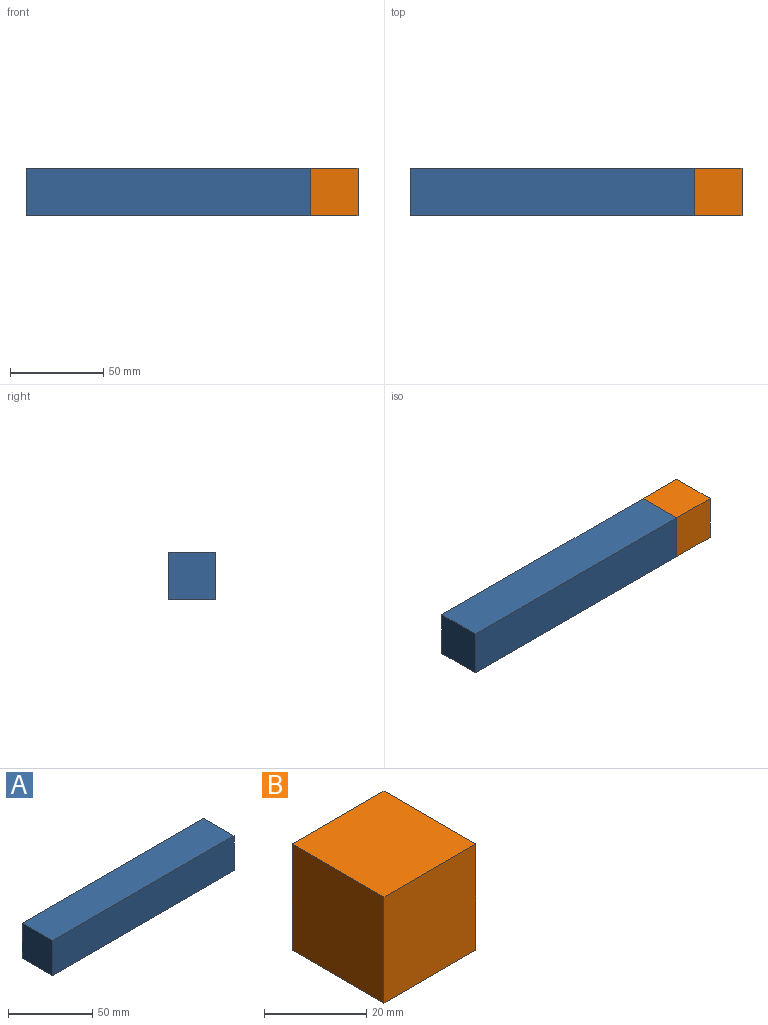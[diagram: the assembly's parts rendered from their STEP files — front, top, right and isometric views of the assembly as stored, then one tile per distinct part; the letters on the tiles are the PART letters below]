
ASSEMBLY  parts=2 mates=1
PART A: 6 faces, bbox 152.4x25.4x25.4 mm
  f0: plane 152.4x25.4mm, normal (0,0,1), area 3871mm2, adj f1,f3,f4,f5
  f1: plane 25.4x25.4mm, normal (-1,0,0), area 645.2mm2, adj f0,f2,f4,f5
  f2: plane 152.4x25.4mm, normal (0,0,-1), area 3871mm2, adj f1,f3,f4,f5
  f3: plane 25.4x25.4mm, normal (1,0,0), area 645.2mm2, adj f0,f2,f4,f5
  f4: plane 152.4x25.4mm, normal (0,-1,0), area 3871mm2, adj f0,f1,f2,f3
  f5: plane 152.4x25.4mm, normal (0,1,0), area 3871mm2, adj f0,f1,f2,f3
PART B: 6 faces, bbox 25.4x25.4x25.4 mm
  f0: plane 25.4x25.4mm, normal (0,0,1), area 645.2mm2, adj f1,f3,f4,f5
  f1: plane 25.4x25.4mm, normal (-1,0,0), area 645.2mm2, adj f0,f2,f4,f5
  f2: plane 25.4x25.4mm, normal (0,0,-1), area 645.2mm2, adj f1,f3,f4,f5
  f3: plane 25.4x25.4mm, normal (1,0,0), area 645.2mm2, adj f0,f2,f4,f5
  f4: plane 25.4x25.4mm, normal (0,-1,0), area 645.2mm2, adj f0,f1,f2,f3
  f5: plane 25.4x25.4mm, normal (0,1,0), area 645.2mm2, adj f0,f1,f2,f3
PLACE A rot(axis=(-1,0,0),0deg) t=(-69.95,44.86,-6.05)mm
PLACE B rot(axis=(0,-1,0),180deg) t=(252.91,44.86,44.42)mm
MATE slider B.f1 <-> A.f3  axis (1,0,0) through (47.82,32.16,67.21)mm
